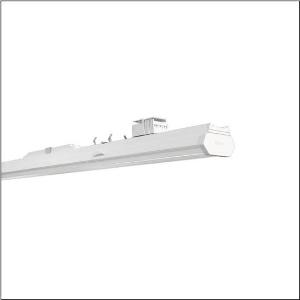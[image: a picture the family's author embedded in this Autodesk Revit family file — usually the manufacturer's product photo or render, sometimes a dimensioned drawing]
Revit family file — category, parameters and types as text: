
# Revit family: licross_r__21_protected_ho_52td12dn4e5m3s4_bb7a
name_source: partatom
category: Lighting Fixtures
units: mm (PartAtom-declared; Revit-internal decimal feet)

## family parameters
Cut with Voids When Loaded = No
Host = Face
Light Source = No
Part Type = Normal
Room Calculation Point = No
Round Connector Dimension = Use Diameter
Shared = No

## types (1)
- --- (1 x LED, 910 lm, 7.6 W, 4000K)
    Apparent Load = 8 VA
    CIE Flux Codes = 70 91 97 98 100
    Color Rendering = 80
    Color Temperature = 4000K
    Default Elevation = 1800 mm
    Description = Licross® 21 Protected HO, luminaire insert, of sheet steel, galvanised, coil coated, white, length: 1.500mm, width: 90mm, height: 103mm, LED rated luminous flux: 14.690lm, light colour: 840, SDCM (Standard Deviation of Colour Matching)MacAdam ≤ 3 SDCM (initial), control gear: DALI 2, with plug, 6-pole, with phase selection, for trunking rail, 9 or 11-core, mains connection: 220..240V, AC, 50/60Hz, rated input power: 89W, for trunking rail, 9-/11-core, internal wiring halogen-free, for emergency light function, converter,control gear: single battery element, battery: LiFePO4, 9Ah, primary light control with lens, of plastic, primary optical cover: cover, of PMMA, light emission: direct distribution, primary light characteristic: symmetric, protection rating (complete): IP54, insulation class (complete): insulation class I (protective earthing), certification: CE, UKCA, protection symbol: D if used in an environment with non-conductive dust loads with corresponding accessories, impact resistance: IK06, permissible ambient temperature for indoor applications: +5..+30°C, standard: EN 60598-2-22, LABS conformity tested according to VDMA 24364:2018-05, reducing of maximum allowable ambient temperature of 5°C with ceiling mounting, corresponds to IFS (International Featured Standards) requirements for safety and quality in the food industry, packaging unit: 1 piece
    Height = 92 mm
    Lamp = 1 x LED
    Lamp Light Flux = 910 lm
    Lamp Power = 7.6 W
    Lamp count = 1
    Length = 1500 mm
    Luminous efficacy = 120 lm/W
    Manufacturer = Siteco
    ModVariant = No
    Model = 52TD12DN4E5M3S4
    Mounting Place = Ceiling
    Mounting Type = Pendant
    Number of Poles = 1
    OnlyDefault = Yes
    Power Factor = 1
    Product Name = Licross® 21 Protected HO
    Product group = luminaire insert | ceiling pendant
    ProductGroupID = 901
    Protection Class = Protection class I
    Protection Degree = IP 54
    RLX_Detail_Level = 1
    RLX_Emergency_Light_Flux = 0 lm
    RLX_Emergency_Type = 0
    RLX_Emergency_Type_DB = No
    RlxData = <blob elided: 24933 chars, md5=8fcdd1bd>
    Socket = socket
    Standby Power = 0 W
    System Light Flux = 910 lm
    System Power = 8 W
    Type Comments = : emergency light operation: 3 h
    Type Image = l_1256148.jpg
    URL = http://relux.com
    VarID = @adj_115129
    Voltage = 0 V
    Weight = 0.00 kg
    Width = 88 mm

## geometry (parser evidence)
native form markers: Blend x4, Sweep x11
no freeform markers — native parametric forms only
